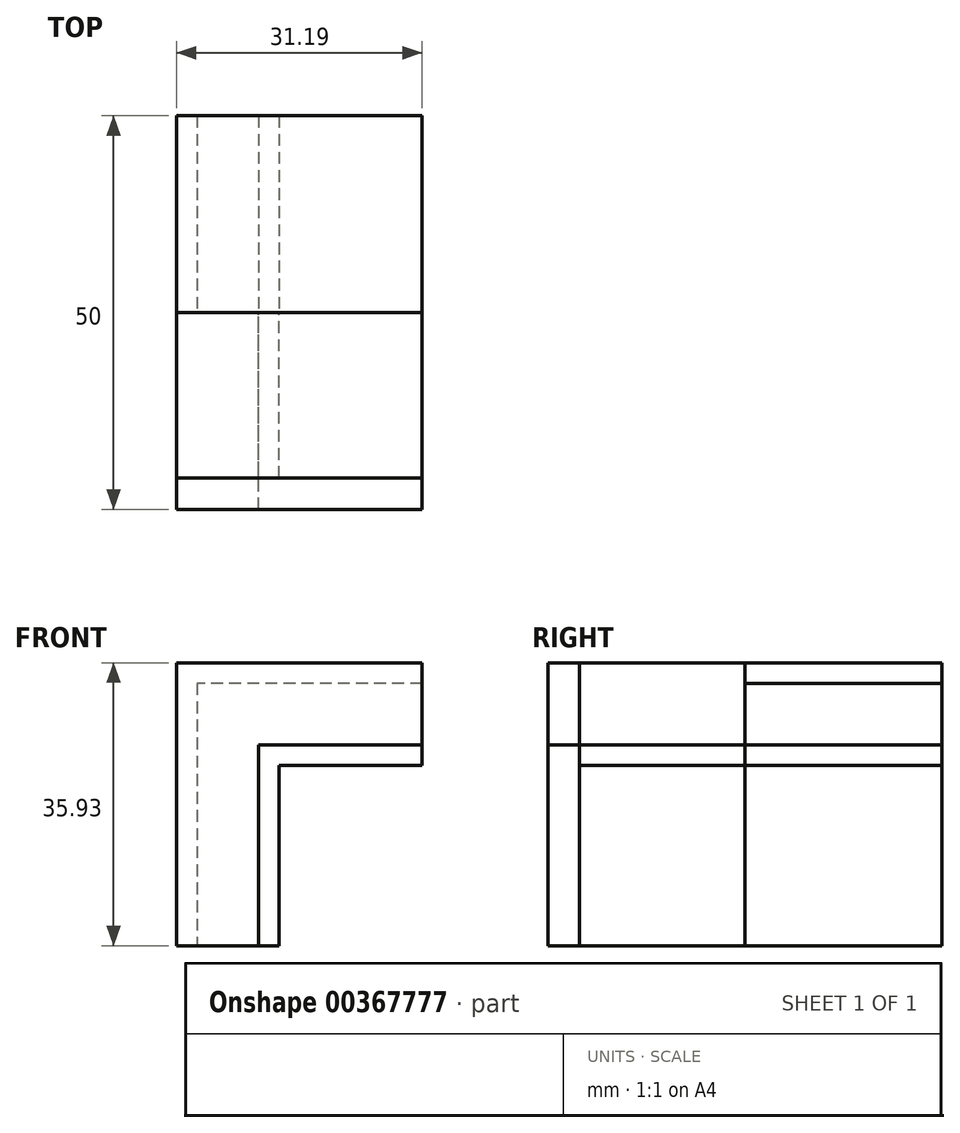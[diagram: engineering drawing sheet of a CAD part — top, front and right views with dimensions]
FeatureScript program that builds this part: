
annotation { "Feature Type Name" : "Feature", "Feature Type Description" : "" }
export const myFeature = defineFeature(function(context is Context, id is Id, definition is map)
    precondition{}
    {
        {
            var Q0;
            Q0=qCreatedBy(makeId("Front.planeOp"),FACE);
            var sketch = newSketch(context, id + "F0", { "sketchPlane" : qUnion([Q0])});
            skLineSegment(sketch, "E0.top", {"start": v(0, -22.93) * mm, "end": v(-13, -22.93) * mm});
            skLineSegment(sketch, "E0.left", {"start": v(0, 0) * mm, "end": v(0, -22.93) * mm});
            skLineSegment(sketch, "E0.right", {"start": v(-13, 0) * mm, "end": v(-13, -22.93) * mm});
            skLineSegment(sketch, "E1.bottom", {"start": v(0, 0) * mm, "end": v(18.2, 0) * mm});
            skLineSegment(sketch, "E1.top", {"start": v(0, 13) * mm, "end": v(18.2, 13) * mm});
            skLineSegment(sketch, "E1.right", {"start": v(18.2, 0) * mm, "end": v(18.2, 13) * mm});
            skLineSegment(sketch, "E2.top", {"start": v(0, 13) * mm, "end": v(-13, 13) * mm});
            skLineSegment(sketch, "E2.right", {"start": v(-13, 0) * mm, "end": v(-13, 13) * mm});
            skLineSegment(sketch, "E3.0", {"start": v(-10.4, 0) * mm, "end": v(-10.4, -22.93) * mm});
            skLineSegment(sketch, "E3.1", {"start": v(-10.4, 0) * mm, "end": v(-10.4, 10.4) * mm});
            skLineSegment(sketch, "E3.2", {"start": v(0, 10.4) * mm, "end": v(-10.4, 10.4) * mm});
            skLineSegment(sketch, "E3.3", {"start": v(0, 10.4) * mm, "end": v(18.2, 10.4) * mm});
            skLineSegment(sketch, "E4.0", {"start": v(-2.6, 2.6) * mm, "end": v(-2.6, -22.93) * mm});
            skLineSegment(sketch, "E4.1", {"start": v(-2.6, 2.6) * mm, "end": v(18.2, 2.6) * mm});
            skSolve(sketch);
        }
        {
            var Q0;
            {var subQ3=sQuery(id+"F0.wireOp",EDGE,"E0.left");Q0=makeQuery(id+"F0.imprint","IMPRINT",FACE,{"disambiguationData":[TD([[makeQuery(id+"F0.imprint","IMPRINT",EDGE,{"derivedFrom":subQ3}),-1.0]])]});}
            var Q1;
            {var subQ3=sQuery(id+"F0.wireOp",EDGE,"E0.right");Q1=makeQuery(id+"F0.imprint","IMPRINT",FACE,{"disambiguationData":[TD([[makeQuery(id+"F0.imprint","IMPRINT",EDGE,{"derivedFrom":subQ3}),1.0]])]});}
            extrude(context, id + "F1", {"entities" : qUnion([Q0, Q1]), "depth" : -25 * mm});
        }
        {
            var Q0;
            {var subQ0=sQuery(id+"F0.wireOp",EDGE,"E3.0");Q0=makeQuery(id+"F0.imprint","IMPRINT",FACE,{"disambiguationData":[TD([[makeQuery(id+"F0.imprint","IMPRINT",EDGE,{"derivedFrom":subQ0}),1.0]])]});}
            var Q1;
            {var subQ3=sQuery(id+"F0.wireOp",EDGE,"E0.right");Q1=makeQuery(id+"F0.imprint","IMPRINT",FACE,{"disambiguationData":[TD([[makeQuery(id+"F0.imprint","IMPRINT",EDGE,{"derivedFrom":subQ3}),1.0]])]});}
            extrude(context, id + "F2", {"entities" : qUnion([Q0, Q1]), "operationType" : NewBodyOperationType.ADD, "depth" : 25 * mm});
        }
        {
            var Q0;
            Q0 = qSketchRegion(id + "F0", true);
            var Q1;
            Q1=makeQuery(id+"F1.opExtrude","CAP_FACE",FACE,{"disambiguationData":[OSD([sQuery(id+"F0.wireOp",EDGE,"E0.top"),sQuery(id+"F0.wireOp",EDGE,"E0.left"),sQuery(id+"F0.wireOp",EDGE,"E1.bottom"),sQuery(id+"F0.wireOp",EDGE,"E1.right"),sQuery(id+"F0.wireOp",EDGE,"E4.0"),sQuery(id+"F0.wireOp",EDGE,"E4.1")])],"isStart":true});
            extrude(context, id + "F3", {"entities" : qUnion([Q0, Q1]), "depth" : 21 * mm});
        }
    });
